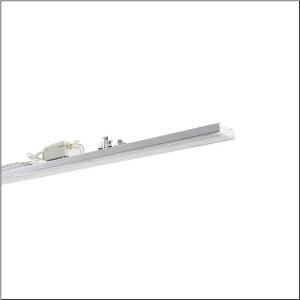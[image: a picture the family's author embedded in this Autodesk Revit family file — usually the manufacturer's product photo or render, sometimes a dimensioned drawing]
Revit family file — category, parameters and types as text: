
# Revit family: licross_r__11_recessed_ho_51tl12dn4exm3s_95e2
name_source: partatom
category: Lighting Fixtures
units: mm (PartAtom-declared; Revit-internal decimal feet)

## family parameters
Cut with Voids When Loaded = No
Host = Face
Light Source = No
Part Type = Normal
Room Calculation Point = No
Round Connector Dimension = Use Diameter
Shared = No

## types (1)
- --- (1 x LED, 1000 lm, 7.2 W, 4000K)
    Apparent Load = 7 VA
    CIE Flux Codes = 66 91 98 100 100
    Color Rendering = 80
    Color Temperature = 4000K
    Default Elevation = 1800 mm
    Description = Licross® 11 Recessed HO, luminaire insert, of sheet steel, coil coated, white, length: 1.500mm, width: 66mm, height: 67mm, LED rated luminous flux: 14.030lm, light colour: 840, control gear: DALI 2 (for two DALI lines), with plug, 6-pole, with phase selection, for trunking rail, 14-core, mains connection: 220..240V, AC, 50/60Hz, rated input power: 81W, for trunking rail, 14-core, halogen-free wiring, for emergency light function, converter,control gear: single battery element, battery: LiFePO4, 9Ah, primary optical cover: cover, of PMMA, light emission: direct distribution, primary light characteristic: symmetric, protection rating (complete): IP40, insulation class (complete): insulation class I (protective earthing), certification: CE, UKCA, protection symbol: D if used in an environment without relevant dust loads with corresponding accessories, impact resistance: IK06, permissible ambient temperature for indoor applications: +5..+30°C, standard: EN 60598-2-22, LABS conformity tested according to VDMA 24364:2018-05, reducing of maximum allowable ambient temperature of 5°C with ceiling mounting, corresponds to IFS (International Featured Standards) requirements for safety and quality in the food industry, packaging unit: 1 piece
    Height = 58 mm
    Lamp = 1 x LED
    Lamp Light Flux = 1000 lm
    Lamp Power = 7.2 W
    Lamp count = 1
    Length = 1500 mm
    Luminous efficacy = 139 lm/W
    Manufacturer = Siteco
    ModVariant = No
    Model = 51TL12DN4EXM3S
    Mounting Place = Ceiling
    Mounting Type = Pendant
    Number of Poles = 1
    OnlyDefault = Yes
    Power Factor = 1
    Product Name = Licross® 11 Recessed HO
    Product group = luminaire insert
    ProductGroupID = 901
    Protection Class = Protection class I
    Protection Degree = IP 40
    RLX_Detail_Level = 1
    RLX_Emergency_Light_Flux = 0 lm
    RLX_Emergency_Type = 0
    RLX_Emergency_Type_DB = No
    RlxData = <blob elided: 24953 chars, md5=551cd662>
    Socket = socket
    Standby Power = 0 W
    System Light Flux = 1000 lm
    System Power = 7 W
    Type Comments = : emergency light operation: 3 h
    Type Image = l_1296930.jpg
    URL = http://relux.com
    VarID = @adj_058849
    Voltage = 0 V
    Weight = 0.00 kg
    Width = 66 mm

## geometry (parser evidence)
native form markers: Blend x4, Sweep x10
no freeform markers — native parametric forms only
